# Revit family: Deca_Monocomando de Cozinha Filtros Cozinha_2240.C_Filtro Twin Mesa
name_source: partatom
category: Plumbing Fixtures
revit_build: Autodesk Revit Architecture 2012 (Build: 20110916_2132(x64)
units: mm (PartAtom-declared; Revit-internal decimal feet)

## types (1)
- 2240.C_Cromado CR10
    Acompanha do Producto = Ligação Flexível: 40 cm
    Assembly Code = D2020
    Atendimento ao Cliente = 0800-011-7073
    CWFU = 0
    Consumo = Varia com a pressão
    Código = 2240.C
    Default Elevation = 0 mm  [stored 0 ft]
    Description = Monocomando com filtro cozinha mesa
    Diâmetro Água Fria = 15 mm  [stored 0.0492126 ft]
    Diâmetro Água Quente = 15 mm  [stored 0.0492126 ft]
    Flow Pressure = 0.00 psi
    HWFU = 0
    Informações Complementares = Mecanismo: 1/4 de volta
    Linha = Filtros Cozinha
    Louça/Metais = Metal
    Manufacturer = Deca
    Material = Deca_Latão Cromado e Plástico de Engenharia
    Model = 2240.C
    Monocomando = Deca CR10 Cromado Metal
    Norma = ABNT NBR 15267: 2005
    Peso Liquido (Kg) = 3.3
    Pressão = 2 A 40 mca
    Produto = Monocomando de Cozinha com filtro Twin - Mesa
    Raio Água Fria = 8 mm  [stored 0.0262467 ft]
    Raio Água Quente = 8 mm  [stored 0.0262467 ft]
    Segmento = Médio
    URL = www.deca.com.br/produtos
    Variações de COR = Cromado (2240.C).

note: [stored X ft] marks values corroborated as IEEE doubles in the binary element streams (Revit-internal decimal feet)

## geometry (parser evidence)
native form markers: Blend x4, Sweep x1
no freeform markers — native parametric forms only
